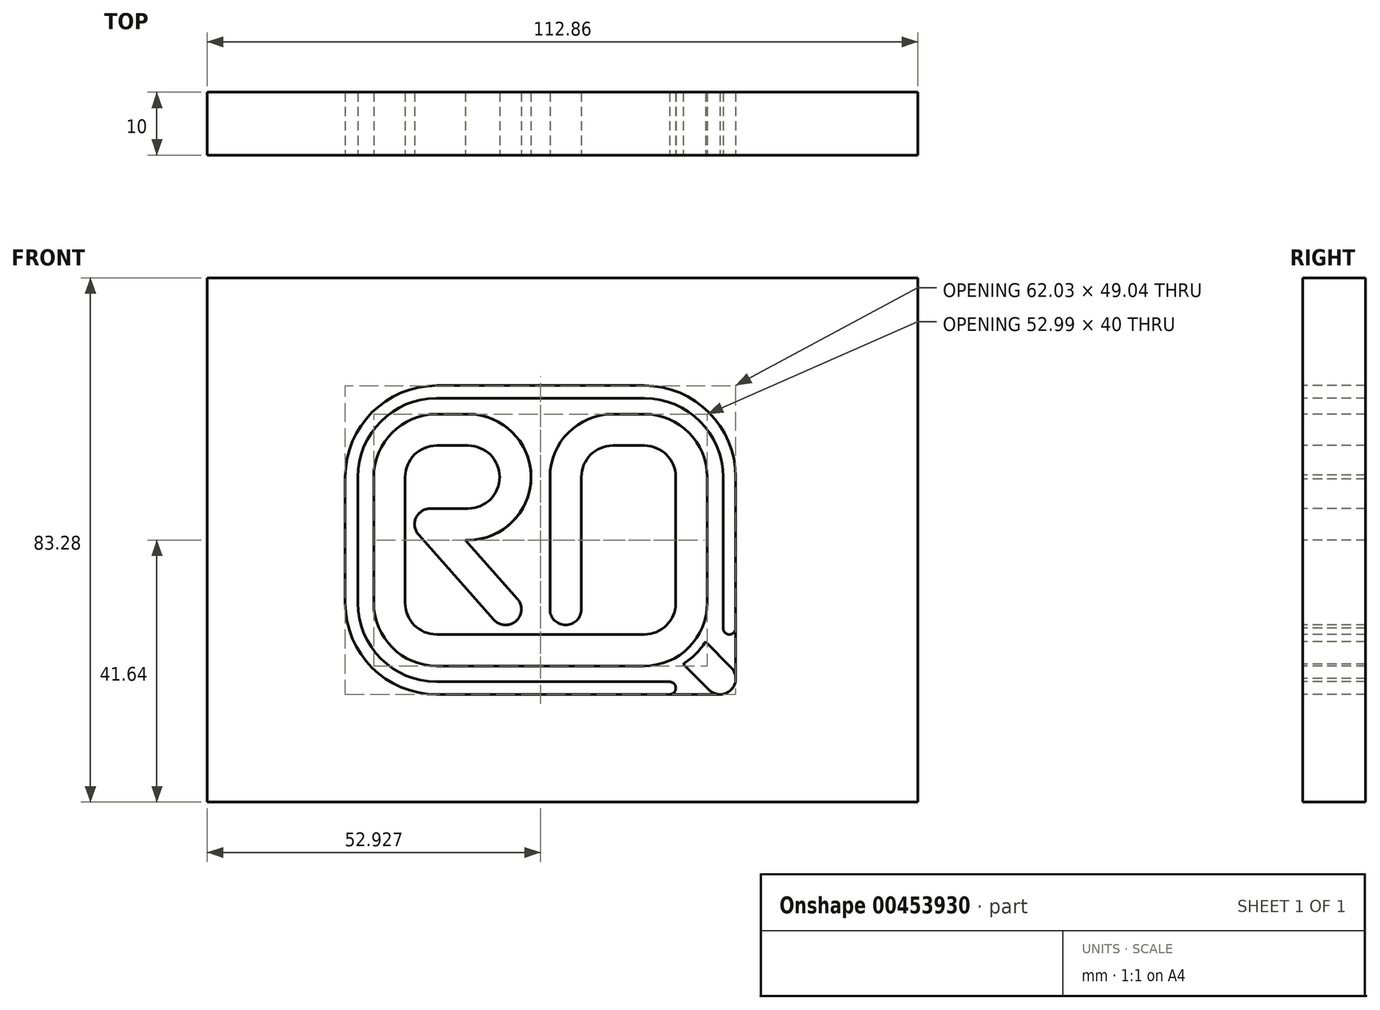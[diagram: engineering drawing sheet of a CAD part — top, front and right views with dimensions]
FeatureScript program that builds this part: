
annotation { "Feature Type Name" : "Feature", "Feature Type Description" : "" }
export const myFeature = defineFeature(function(context is Context, id is Id, definition is map)
    precondition{}
    {
        {
            var Q0;
            Q0=qCreatedBy(makeId("Front.planeOp"),FACE);
            var sketch = newSketch(context, id + "F0", { "sketchPlane" : qUnion([Q0])});
            skPoint(sketch, "E0.middle", {"position": v(0, 0) * mm});
            skLineSegment(sketch, "E1", {"start": v(-25, 10) * mm, "end": v(-25, -10) * mm});
            skLineSegment(sketch, "E2", {"start": v(-2, -20) * mm, "end": v(-0.38, -20) * mm});
            skLineSegment(sketch, "E3", {"start": v(-2, -11) * mm, "end": v(-2, 10) * mm});
            skLineSegment(sketch, "E4", {"start": v(8, 20) * mm, "end": v(13, 20) * mm});
            skLineSegment(sketch, "E5", {"start": v(23, 10) * mm, "end": v(23, -10) * mm});
            skLineSegment(sketch, "E6", {"start": v(13, -20) * mm, "end": v(9, -20) * mm});
            skLineSegment(sketch, "E7", {"start": v(-25, 20) * mm, "end": v(-15, 20) * mm});
            skLineSegment(sketch, "E8", {"start": v(-21, 0) * mm, "end": v(-15, 0) * mm});
            skLineSegment(sketch, "E9", {"start": v(-5, 10.33) * mm, "end": v(-5, 10.33) * mm});
            skPoint(sketch, "E10.visualSharp", {"position": v(-5.33, 20) * mm});
            skArc(sketch, "E10.filletArc", {"start": v(-5, 10.33) * mm, "mid": v(-8.05, 17.19) * mm, "end": v(-15, 20) * mm});
            skArc(sketch, "E11.filletArc", {"start": v(-15, 0) * mm, "mid": v(-7.81, 3.05) * mm, "end": v(-5, 10.33) * mm});
            skPoint(sketch, "E12.visualSharp", {"position": v(-3.63, -20) * mm});
            skPoint(sketch, "E13.visualSharp", {"position": v(23, -20) * mm});
            skArc(sketch, "E13.filletArc", {"start": v(13, -20) * mm, "mid": v(20.07, -17.07) * mm, "end": v(23, -10) * mm});
            skPoint(sketch, "E14.visualSharp", {"position": v(23, 20) * mm});
            skArc(sketch, "E14.filletArc", {"start": v(23, 10) * mm, "mid": v(20.07, 17.07) * mm, "end": v(13, 20) * mm});
            skPoint(sketch, "E15.visualSharp", {"position": v(-2, 20) * mm});
            skArc(sketch, "E15.filletArc", {"start": v(8, 20) * mm, "mid": v(0.92, 17.07) * mm, "end": v(-2, 10) * mm});
            skPoint(sketch, "E16.visualSharp", {"position": v(-2, -20) * mm});
            skArc(sketch, "E17.0", {"start": v(8, 15) * mm, "mid": v(4.46, 13.54) * mm, "end": v(3, 10) * mm});
            skLineSegment(sketch, "E17.1", {"start": v(3, -11) * mm, "end": v(3, 10) * mm});
            skLineSegment(sketch, "E17.2", {"start": v(8, 15) * mm, "end": v(13, 15) * mm});
            skArc(sketch, "E17.4", {"start": v(18, 10) * mm, "mid": v(16.53, 13.54) * mm, "end": v(13, 15) * mm});
            skLineSegment(sketch, "E17.5", {"start": v(18, 10) * mm, "end": v(18, -10) * mm});
            skArc(sketch, "E17.6", {"start": v(13, -15) * mm, "mid": v(16.53, -13.54) * mm, "end": v(18, -10) * mm});
            skLineSegment(sketch, "E17.7", {"start": v(13, -15) * mm, "end": v(9, -15) * mm});
            skArc(sketch, "E18.1", {"start": v(-15, 5) * mm, "mid": v(-11.44, 6.5) * mm, "end": v(-10, 10.08) * mm});
            skArc(sketch, "E18.2", {"start": v(-10, 10.08) * mm, "mid": v(-11.5, 13.56) * mm, "end": v(-15, 15) * mm});
            skLineSegment(sketch, "E18.3", {"start": v(-20, 15) * mm, "end": v(-15, 15) * mm});
            skLineSegment(sketch, "E19.0", {"start": v(-30, 17.5) * mm, "end": v(-30, -10) * mm});
            skLineSegment(sketch, "E20.0", {"start": v(-1, -15) * mm, "end": v(-0.38, -15) * mm});
            skLineSegment(sketch, "E21", {"start": v(-20, -20) * mm, "end": v(-2, -20) * mm});
            skLineSegment(sketch, "E22", {"start": v(-1, -15) * mm, "end": v(9, -15) * mm});
            skLineSegment(sketch, "E23.0", {"start": v(-20, -15) * mm, "end": v(0, -15) * mm});
            skLineSegment(sketch, "E24", {"start": v(-5, 10.33) * mm, "end": v(-5, 0) * mm});
            skLineSegment(sketch, "E25", {"start": v(0.5, -13.5) * mm, "end": v(0.5, -13.5) * mm});
            skPoint(sketch, "E26.visualSharp", {"position": v(3, -13.5) * mm});
            skArc(sketch, "E26.filletArc", {"start": v(0.5, -13.5) * mm, "mid": v(2.26, -12.77) * mm, "end": v(3, -11) * mm});
            skPoint(sketch, "E27.newPointB", {"position": v(-23.5, -13.5) * mm});
            skArc(sketch, "E27.filletArc", {"start": v(-2, -11) * mm, "mid": v(-1.27, -12.77) * mm, "end": v(0.5, -13.5) * mm});
            skPoint(sketch, "E28.visualSharp", {"position": v(-30, -20) * mm});
            skArc(sketch, "E28.filletArc", {"start": v(-30, -19.5) * mm, "mid": v(-29.85, -19.85) * mm, "end": v(-29.5, -20) * mm});
            skLineSegment(sketch, "E29", {"start": v(-7.28, -12.77) * mm, "end": v(-7.28, -12.77) * mm});
            skArc(sketch, "E30.filletArc", {"start": v(-7.28, -12.77) * mm, "mid": v(-6.55, -11) * mm, "end": v(-7.27, -9.24) * mm});
            skArc(sketch, "E31.filletArc", {"start": v(-11.23, -12.21) * mm, "mid": v(-9.4, -13.48) * mm, "end": v(-7.28, -12.77) * mm});
            skLineSegment(sketch, "E32.0", {"start": v(19.16, -19.7) * mm, "end": v(23.25, -23.79) * mm});
            skLineSegment(sketch, "E33.0", {"start": v(22.7, -16.17) * mm, "end": v(26.78, -20.25) * mm});
            skLineSegment(sketch, "E34.0", {"start": v(14.76, -15.3) * mm, "end": v(14.29, -14.83) * mm});
            skPoint(sketch, "E35.newPointB", {"position": v(-25, 20) * mm});
            skPoint(sketch, "E36.visualSharp", {"position": v(-23.5, 5) * mm});
            skPoint(sketch, "E37.visualSharp", {"position": v(-23.5, 0) * mm});
            skLineSegment(sketch, "E38", {"start": v(-30, 10) * mm, "end": v(-30, 17.5) * mm});
            skLineSegment(sketch, "E39", {"start": v(-20, 20) * mm, "end": v(-25, 20) * mm});
            skPoint(sketch, "E40.visualSharp", {"position": v(-30, 20) * mm});
            skArc(sketch, "E40.filletArc", {"start": v(-20, 20) * mm, "mid": v(-27.07, 17.07) * mm, "end": v(-30, 10) * mm});
            skArc(sketch, "E41", {"start": v(23.25, -23.79) * mm, "mid": v(26.78, -23.79) * mm, "end": v(26.78, -20.25) * mm});
            skPoint(sketch, "E42", {"position": v(20.07, -17.07) * mm});
            skPoint(sketch, "E43.orphan", {"position": v(16.53, -13.54) * mm});
            skLineSegment(sketch, "E44.trimOffspring", {"start": v(13, -20) * mm, "end": v(-0.38, -20) * mm});
            skArc(sketch, "E45.trimOffspring", {"start": v(19.16, -19.7) * mm, "mid": v(21.13, -18.13) * mm, "end": v(22.7, -16.17) * mm});
            skPoint(sketch, "E46.newPointB", {"position": v(-25, -20) * mm});
            skArc(sketch, "E46.filletArc", {"start": v(-25, -10) * mm, "mid": v(-23.54, -13.54) * mm, "end": v(-20, -15) * mm});
            skLineSegment(sketch, "E47", {"start": v(-15, 20) * mm, "end": v(8, 20) * mm});
            skLineSegment(sketch, "E48", {"start": v(21.86, -24.52) * mm, "end": v(-20, -24.52) * mm});
            skLineSegment(sketch, "E49", {"start": v(27.51, -22.02) * mm, "end": v(27.51, -18.86) * mm});
            skLineSegment(sketch, "E50", {"start": v(13, 24.52) * mm, "end": v(-20, 24.52) * mm});
            skLineSegment(sketch, "E51", {"start": v(-34.52, -10) * mm, "end": v(-34.52, 10) * mm});
            skPoint(sketch, "E52.orphan", {"position": v(17.43, -17.97) * mm});
            skPoint(sketch, "E53.orphan", {"position": v(13.35, -13.89) * mm});
            skArc(sketch, "E54.0", {"start": v(27.51, 10) * mm, "mid": v(23.26, 20.27) * mm, "end": v(13, 24.52) * mm});
            skArc(sketch, "E55.0", {"start": v(25.51, 10) * mm, "mid": v(21.85, 18.85) * mm, "end": v(13, 22.52) * mm});
            skLineSegment(sketch, "E56.0", {"start": v(25.51, -22.07) * mm, "end": v(25.51, -18.99) * mm});
            skLineSegment(sketch, "E57.0", {"start": v(25.02, -22.52) * mm, "end": v(21.98, -22.52) * mm});
            skLineSegment(sketch, "E58.0", {"start": v(-32.52, -10) * mm, "end": v(-32.52, 10) * mm});
            skLineSegment(sketch, "E59.0", {"start": v(13, 22.52) * mm, "end": v(-20, 22.52) * mm});
            skPoint(sketch, "E60.visualSharp", {"position": v(-32.52, 22.52) * mm});
            skArc(sketch, "E60.filletArc", {"start": v(-20, 22.52) * mm, "mid": v(-28.85, 18.85) * mm, "end": v(-32.52, 10) * mm});
            skArc(sketch, "E61.0", {"start": v(-20, 24.52) * mm, "mid": v(-30.27, 20.27) * mm, "end": v(-34.52, 10) * mm});
            skPoint(sketch, "E62.visualSharp", {"position": v(-32.52, -22.52) * mm});
            skLineSegment(sketch, "E63", {"start": v(26.51, -15) * mm, "end": v(26.51, -16.32) * mm});
            skLineSegment(sketch, "E64.0", {"start": v(18.1, -20.77) * mm, "end": v(22.19, -24.85) * mm, "construction": true});
            skLineSegment(sketch, "E65.0", {"start": v(23.76, -15.1) * mm, "end": v(27.84, -19.2) * mm, "construction": true});
            skArc(sketch, "E66", {"start": v(17, -24.52) * mm, "mid": v(18, -23.52) * mm, "end": v(17, -22.52) * mm});
            skCircle(sketch, "E67", {"center": v(26.51, -14) * mm, "radius": 1 * mm});
            skLineSegment(sketch, "E68.trimOffspring", {"start": v(25.51, -14) * mm, "end": v(25.51, 10) * mm});
            skLineSegment(sketch, "E69.trimOffspring", {"start": v(27.51, -14) * mm, "end": v(27.51, 33) * mm});
            skLineSegment(sketch, "E70.trimOffspring", {"start": v(19.86, -22.52) * mm, "end": v(-20, -22.52) * mm});
            skLineSegment(sketch, "E71", {"start": v(21.86, -24.52) * mm, "end": v(25.02, -24.52) * mm});
            skLineSegment(sketch, "E72", {"start": v(27.51, -14) * mm, "end": v(27.51, -22.02) * mm});
            skLineSegment(sketch, "E73.bottom", {"start": v(-56.43, 41.64) * mm, "end": v(56.43, 41.64) * mm});
            skLineSegment(sketch, "E73.top", {"start": v(-56.43, -41.64) * mm, "end": v(56.43, -41.64) * mm});
            skLineSegment(sketch, "E73.left", {"start": v(-56.43, 41.64) * mm, "end": v(-56.43, -41.64) * mm});
            skLineSegment(sketch, "E73.right", {"start": v(56.43, 41.64) * mm, "end": v(56.43, -41.64) * mm});
            skLineSegment(sketch, "E74", {"start": v(0, 0) * mm, "end": v(0, -38.7) * mm, "construction": true});
            skLineSegment(sketch, "E75", {"start": v(0, 0) * mm, "end": v(33.56, 0) * mm, "construction": true});
            skArc(sketch, "E76.filletArc", {"start": v(-20, 15) * mm, "mid": v(-23.54, 13.54) * mm, "end": v(-25, 10) * mm});
            skArc(sketch, "E77.0", {"start": v(-30, -10) * mm, "mid": v(-27.07, -17.07) * mm, "end": v(-20, -20) * mm});
            skArc(sketch, "E78.0", {"start": v(-34.52, -10) * mm, "mid": v(-30.27, -20.27) * mm, "end": v(-20, -24.52) * mm});
            skArc(sketch, "E79.0", {"start": v(-32.52, -10) * mm, "mid": v(-28.85, -18.85) * mm, "end": v(-20, -22.52) * mm});
            skLineSegment(sketch, "E80", {"start": v(-15, 5) * mm, "end": v(-21, 5) * mm});
            skLineSegment(sketch, "E81", {"start": v(-23.5, 2.5) * mm, "end": v(-23.5, 2.5) * mm});
            skArc(sketch, "E82.filletArc", {"start": v(-21, 5) * mm, "mid": v(-22.77, 4.27) * mm, "end": v(-23.5, 2.5) * mm});
            skArc(sketch, "E83.filletArc", {"start": v(-23.5, 2.5) * mm, "mid": v(-22.77, 0.73) * mm, "end": v(-21, 0) * mm});
            skLineSegment(sketch, "E84", {"start": v(-11.23, -12.21) * mm, "end": v(-18, 0) * mm, "construction": true});
            skPoint(sketch, "E85.startSnap0", {"position": v(-6.55, -11) * mm});
            skLineSegment(sketch, "E86.0", {"start": v(-6.86, -9.79) * mm, "end": v(-13.63, 2.42) * mm, "construction": true});
            skLineSegment(sketch, "E87", {"start": v(-22.87, 0.84) * mm, "end": v(-10.92, -12.66) * mm});
            skLineSegment(sketch, "E88.0", {"start": v(-19.13, 4.16) * mm, "end": v(-7.17, -9.34) * mm});
            skSolve(sketch);
        }
        {
            var Q0;
            Q0=makeQuery(id+"F0.imprint","IMPRINT",FACE,{"disambiguationData":[TD([[makeQuery(id+"F0.imprint","IMPRINT",EDGE,{"derivedFrom":sQuery(id+"F0.wireOp",EDGE,"E1")}),-1.0]])]});
            var Q1;
            {var subQ6=sQuery(id+"F0.wireOp",EDGE,"8dgEX87s-OnN3-UPAw-RyUf-tcfM0RuKeMZf");Q1=makeQuery(id+"F0.imprint","IMPRINT",FACE,{"disambiguationData":[TD([[makeQuery(id+"F0.imprint","IMPRINT",EDGE,{"derivedFrom":subQ6}),1.0]])]});}
            var Q2;
            {var subQ0=sQuery(id+"F0.wireOp",EDGE,"E41");var subQ1=makeQuery(id+"F0.imprint","INTERSECT",VERTEX,{"derivedFrom":[sQuery(id+"F0.wireOp",EDGE,"E33.0"),subQ0]});Q2=makeQuery(id+"F0.imprint","IMPRINT",FACE,{"disambiguationData":[TD([[makeQuery(id+"F0.imprint","IMPRINT",EDGE,{"disambiguationData":[TD([[subQ1,-1.0]])],"derivedFrom":subQ0}),1.0]])]});}
            var Q3;
            {var subQ1=sQuery(id+"F0.wireOp",EDGE,"E33.0");Q3=makeQuery(id+"F0.imprint","IMPRINT",FACE,{"disambiguationData":[TD([[makeQuery(id+"F0.imprint","IMPRINT",EDGE,{"derivedFrom":subQ1}),-1.0]])]});}
            var Q4;
            {var subQ0=sQuery(id+"F0.wireOp",EDGE,"E0.bottom");Q4=makeQuery(id+"F0.imprint","IMPRINT",FACE,{"disambiguationData":[TD([[makeQuery(id+"F0.imprint","IMPRINT",EDGE,{"derivedFrom":subQ0}),-1.0]])]});}
            var Q5;
            {var subQ0=sQuery(id+"F0.wireOp",EDGE,"E0.bottom");Q5=makeQuery(id+"F0.imprint","IMPRINT",FACE,{"disambiguationData":[TD([[makeQuery(id+"F0.imprint","IMPRINT",EDGE,{"derivedFrom":subQ0}),1.0]])]});}
            var Q6;
            {var subQ0=sQuery(id+"F0.wireOp",EDGE,"E31.filletArc");Q6=makeQuery(id+"F0.imprint","IMPRINT",FACE,{"disambiguationData":[TD([[makeQuery(id+"F0.imprint","IMPRINT",EDGE,{"derivedFrom":subQ0}),1.0]])]});}
            extrude(context, id + "F1", {"entities" : qUnion([Q0, Q1, Q2, Q3, Q4, Q5, Q6]), "oppositeDirection" : true, "depth" : 10 * mm});
        }
        {
            var Q0;
            Q0=makeQuery(id+"F0.imprint","IMPRINT",FACE,{"disambiguationData":[TD([[makeQuery(id+"F0.imprint","IMPRINT",EDGE,{"derivedFrom":sQuery(id+"F0.wireOp",EDGE,"E1")}),1.0]])]});
            var Q1;
            {var subQ16=sQuery(id+"F0.wireOp",EDGE,"E2");Q1=makeQuery(id+"F0.imprint","IMPRINT",FACE,{"disambiguationData":[TD([[makeQuery(id+"F0.imprint","IMPRINT",EDGE,{"derivedFrom":subQ16}),-1.0]])]});}
            extrude(context, id + "F2", {"entities" : qUnion([Q0, Q1]), "oppositeDirection" : true, "depth" : 10 * mm});
        }
        {
            var Q0;
            Q0=makeQuery(id+"F0.imprint","IMPRINT",FACE,{"disambiguationData":[TD([[makeQuery(id+"F0.imprint","IMPRINT",EDGE,{"derivedFrom":sQuery(id+"F0.wireOp",EDGE,"E50")}),1.0]])]});
            var Q1;
            {var subQ0=sQuery(id+"F0.wireOp",EDGE,"E66");var subQ2=makeQuery(id+"F0.imprint","IMPRINT",VERTEX,{"derivedFrom":subQ0});Q1=makeQuery(id+"F0.imprint","IMPRINT",FACE,{"disambiguationData":[TD([[makeQuery(id+"F0.imprint","IMPRINT",EDGE,{"disambiguationData":[TD([[subQ2,-1.0]])],"derivedFrom":subQ0}),1.0]])]});}
            var Q2;
            {var subQ0=sQuery(id+"F0.wireOp",EDGE,"E67");var subQ3=makeQuery(id+"F0.imprint","IMPRINT",VERTEX,{"derivedFrom":subQ0});Q2=makeQuery(id+"F0.imprint","IMPRINT",FACE,{"disambiguationData":[TD([[makeQuery(id+"F0.imprint","IMPRINT",EDGE,{"disambiguationData":[TD([[subQ3,1.0]])],"derivedFrom":subQ0}),1.0]])]});}
            extrude(context, id + "F3", {"entities" : qUnion([Q0, Q1, Q2]), "oppositeDirection" : true, "depth" : 10 * mm});
        }
        {
            var Q0;
            Q0=makeQuery(id+"F0.imprint","IMPRINT",FACE,{"disambiguationData":[TD([[makeQuery(id+"F0.imprint","IMPRINT",EDGE,{"derivedFrom":sQuery(id+"F0.wireOp",EDGE,"E50")}),-1.0]])]});
            extrude(context, id + "F4", {"entities" : qUnion([Q0]), "oppositeDirection" : true, "depth" : 10 * mm});
        }
    });
